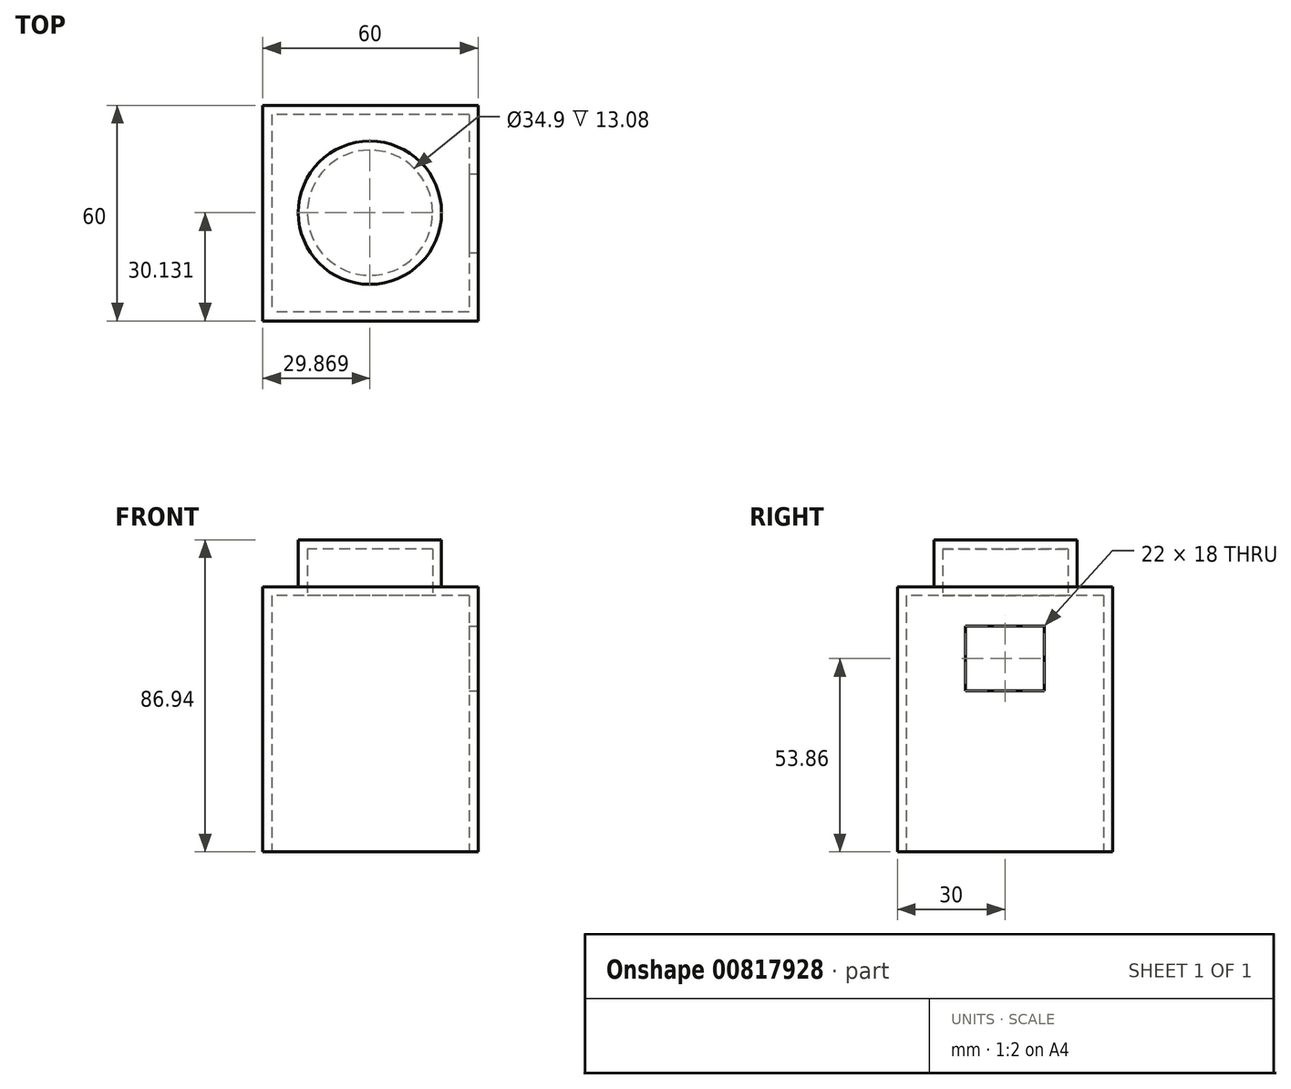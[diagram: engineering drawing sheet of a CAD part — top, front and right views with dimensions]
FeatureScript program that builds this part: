
annotation { "Feature Type Name" : "Feature", "Feature Type Description" : "" }
export const myFeature = defineFeature(function(context is Context, id is Id, definition is map)
    precondition{}
    {
        {
            assignVariable(context, id + "F0", {"name" : "Square", "anyValue" : 60});
        }
        {
            assignVariable(context, id + "F1", {"name" : "Height", "anyValue" : 1.23 * getVariable(context, 'Square')});
        }
        {
            assignVariable(context, id + "F2", {"name" : "Step", "anyValue" : .218 * getVariable(context, 'Square')});
        }
        {
            var Q0;
            Q0=qCreatedBy(makeId("Top.planeOp"),FACE);
            var sketch = newSketch(context, id + "F3", { "sketchPlane" : qUnion([Q0])});
            skLineSegment(sketch, "E0.bottom", {"start": v(30, 30) * mm, "end": v(-30, 30) * mm});
            skLineSegment(sketch, "E0.top", {"start": v(30, -30) * mm, "end": v(-30, -30) * mm});
            skLineSegment(sketch, "E0.left", {"start": v(30, 30) * mm, "end": v(30, -30) * mm});
            skLineSegment(sketch, "E0.right", {"start": v(-30, 30) * mm, "end": v(-30, -30) * mm});
            skPoint(sketch, "E0.middle", {"position": v(0, 0) * mm});
            skSolve(sketch);
        }
        {
            var Q0;
            Q0 = qSketchRegion(id + "F3", true);
            extrude(context, id + "F4", {"entities" : qUnion([Q0]), "depth" : (getVariable(context, 'Height')) * mm, "offsetDistance" : 25 * mm});
        }
        {
            var Q0;
            Q0=makeQuery(id+"F4.opExtrude","CAP_FACE",FACE,{"disambiguationData":[OSD([sQuery(id+"F3.wireOp",EDGE,"E0.bottom"),sQuery(id+"F3.wireOp",EDGE,"E0.top"),sQuery(id+"F3.wireOp",EDGE,"E0.left"),sQuery(id+"F3.wireOp",EDGE,"E0.right")])],"isStart":false});
            var sketch = newSketch(context, id + "F5", { "sketchPlane" : qUnion([Q0])});
            skCircle(sketch, "E1", {"center": v(-0.13, 0.13) * mm, "radius": 19.95 * mm});
            skSolve(sketch);
        }
        {
            var Q0;
            Q0=makeQuery(id+"F5.imprint","IMPRINT",FACE,{"disambiguationData":[TD([[makeQuery(id+"F5.imprint","IMPRINT",EDGE,{"derivedFrom":sQuery(id+"F5.wireOp",EDGE,"E1")}),1.0]])]});
            extrude(context, id + "F6", {"entities" : qUnion([Q0]), "operationType" : NewBodyOperationType.ADD, "depth" : (getVariable(context, 'Step')) * mm, "offsetDistance" : 25 * mm});
        }
        {
            var Q0;
            Q0=makeQuery(id+"F4.opExtrude","SWEPT_FACE",FACE,{"disambiguationData":[OSD([sQuery(id+"F3.wireOp",EDGE,"E0.left")])]});
            var sketch = newSketch(context, id + "F7", { "sketchPlane" : qUnion([Q0])});
            skLineSegment(sketch, "E2.bottom", {"start": v(11, 62.86) * mm, "end": v(-11, 62.86) * mm});
            skLineSegment(sketch, "E2.top", {"start": v(11, 44.86) * mm, "end": v(-11, 44.86) * mm});
            skLineSegment(sketch, "E2.left", {"start": v(11, 62.86) * mm, "end": v(11, 44.86) * mm});
            skLineSegment(sketch, "E2.right", {"start": v(-11, 62.86) * mm, "end": v(-11, 44.86) * mm});
            skPoint(sketch, "E2.middle", {"position": v(0, 53.86) * mm});
            skSolve(sketch);
        }
        {
            var Q0;
            Q0=makeQuery(id+"F4.opExtrude","CAP_FACE",FACE,{"disambiguationData":[OSD([sQuery(id+"F3.wireOp",EDGE,"E0.bottom"),sQuery(id+"F3.wireOp",EDGE,"E0.top"),sQuery(id+"F3.wireOp",EDGE,"E0.left"),sQuery(id+"F3.wireOp",EDGE,"E0.right")])],"isStart":true});
            shell(context, id + "F8", {"entities" : qUnion([Q0]), "thickness" : 2.5 * mm});
        }
        {
            var Q0;
            Q0=makeQuery(id+"F7.imprint","IMPRINT",FACE,{"disambiguationData":[TD([[makeQuery(id+"F7.imprint","IMPRINT",EDGE,{"derivedFrom":sQuery(id+"F7.wireOp",EDGE,"E2.bottom")}),1.0]])]});
            extrude(context, id + "F9", {"entities" : qUnion([Q0]), "operationType" : NewBodyOperationType.REMOVE, "oppositeDirection" : true, "depth" : 2.5 * mm, "offsetDistance" : 25 * mm});
        }
    });
